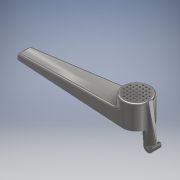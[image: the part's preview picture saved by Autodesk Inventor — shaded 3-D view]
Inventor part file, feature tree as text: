
AUTODESK INVENTOR PART (.ipt)
format: ipt  version: 2018 (Build 220112000, 112)  size: 343,040 bytes
history: native  units: mm
features: extrude x5, sketch x4, fillet x4, shell x2, chamfer x1, loft x1, other x1
ambient origin geometry x8: Origin, YZ Plane, XZ Plane, XY Plane, X Axis, Y Axis, Z Axis, Center Point
bodies: Solid1 (feature_tree)
feature tree (18):
  sketch  "Sketch1"  dims[d0=31.0mm d1=125.0mm d2=8.0mm]
  extrude  "Extrusion1"  Depth=125.0mm
  shell  "Shell1"  Thickness=8.0mm
  extrude  "Extrusion2"  Depth=26.0mm TaperAngle=0.0deg
  chamfer  "Chamfer1"  Distance=15.0mm
  shell  "Shell2"  Thickness=3.0mm
  extrude  "Extrusion3"  Depth=2.0mm
  sketch  "Sketch3"  dims[d6=3.0mm d7=15.0mm d8=0.0mm]
  extrude  "Extrusion4"  Depth=2.0mm
  loft  "Loft1"
  extrude  "Extrusion5"  Depth=10.0mm
  fillet  "Fillet1"  Radius=10.0mm
  fillet  "Fillet2"  Radius=12.75mm
  fillet  "Fillet3"  Radius=3.0mm
  fillet  "Fillet4"  Radius=10.0mm
  sketch  "Sketch2"  dims[d3=8.0mm d4=26.0mm d5=0.0mm]
  sketch  "Sketch4"  dims[d9=124.0mm d10=10.0mm d11=45.0deg d12=3.0mm d25=14.0mm d28=14.0mm d29=2.0mm d33=10.0mm d35=10.0mm d36=80.0mm d38=3.5mm d40=80.0mm d42=3.5mm d43=10.0mm d45=10.0mm d47=12.75mm d48=0.0mm d49=3.0mm d58=10.0mm d59=0.0mm d60=5.0mm d61=5.0mm d62=90.0deg d65=0.0mm d66=10.0mm d68=15.5mm d69=12.5mm d72=0.0mm d73=90.0deg d74=4.0mm d75=0.0mm d80=3.0mm d81=2.0mm d82=2.0mm d85=41.0mm d88=41.0mm d89=4.0mm d90=2.0mm d91=2.0mm d93=0.417424mm d94=2.5mm d95=9.582576mm d96=0.0mm d97=90.0deg d98=2.0mm d99=0.0mm d100=0.0mm d101=2.0mm]
  other  "Edges2"
